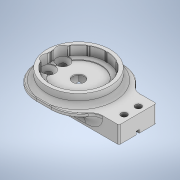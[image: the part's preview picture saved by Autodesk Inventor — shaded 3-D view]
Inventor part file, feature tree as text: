
AUTODESK INVENTOR PART (.ipt)
format: ipt  version: 2022 (Build 260153000, 153)  size: 1,263,104 bytes
history: native  units: mm
features: projected_geometry x17, extrude x13, sketch x12, fillet x8, other x6, pattern_circular x2, chamfer x1, revolve x1, mirror x1
ambient origin geometry x8: Origin, YZ Plane, XZ Plane, XY Plane, X Axis, Y Axis, Z Axis, Center Point
bodies: Body1 (feature_tree)
feature tree (61):
  other  "Твердое тело1"
  extrude  "Выдавливание1"  Depth=21.5mm
  extrude  "Выдавливание2"  Depth=41.0mm
  extrude  "Выдавливание3"  Depth=59.0mm
  extrude  "Выдавливание4"  Depth=10.6mm TaperAngle=0.0deg
  extrude  "Выдавливание5"  Depth=2.0mm
  extrude  "Выдавливание6"  Depth=4.4mm
  fillet  "Сопряжение1"  Radius=10600.0mm
  fillet  "Сопряжение2"  Radius=14.3mm
  fillet  "Сопряжение3"  Radius=10.0mm
  fillet  "Сопряжение4"  Radius=0.9mm
  extrude  "Выдавливание8"  Depth=150.0mm TaperAngle=0.0deg
  fillet  "Сопряжение6"  Radius=37.3mm
  other  "РабОсь1"
  fillet  "Сопряжение8"  Radius=2.5mm
  pattern_circular  "Круговой массив1"  [2 undecoded]
  extrude  "Выдавливание9"  Depth=3.0mm
  extrude  "Выдавливание10"  Depth=2.5mm TaperAngle=0.0deg
  fillet  "Сопряжение9"  Radius=20.0mm
  extrude  "Выдавливание11"  Depth=3.0mm
  chamfer  "Фаска1"  Distance=0.5mm
  extrude  "Выдавливание12"  Depth=1.0mm
  other  "РабОсь2"
  other  "РабПлоскость1"
  sketch  "Эскиз14"
  fillet  "Сопряжение11"  Radius=25.0mm
  extrude  "Выдавливание15"  Depth=0.7mm
  pattern_circular  "Круговой массив3"  Count=12 Angle=360.0deg
  revolve  "Вращение2"
  other  "РабПлоскость2"
  mirror  "Зеркальное отражение1"
  extrude  "Выдавливание17"  Depth=5.0mm TaperAngle=0.0deg
  sketch  "Эскиз1"
  sketch  "Эскиз2"
  sketch  "Эскиз3"
  projected_geometry  "Спроецированная петля1"
  sketch  "Эскиз5"
  projected_geometry  "Спроецированная петля2"
  sketch  "Эскиз6"
  projected_geometry  "Спроецированная петля3"
  projected_geometry  "Спроецированная петля4"
  projected_geometry  "Спроецированная петля5"
  sketch  "Эскиз9"
  sketch  "Эскиз10"
  projected_geometry  "Спроецированная петля6"
  sketch  "Эскиз12"
  projected_geometry  "Спроецированная петля7"
  projected_geometry  "Спроецированная петля8"
  sketch  "Эскиз13"
  other  "РабОсь3"
  sketch  "Эскиз17"
  projected_geometry  "Спроецированная петля9"
  projected_geometry  "Спроецированная петля10"
  projected_geometry  "Спроецированная петля11"
  projected_geometry  "Спроецированная петля12"
  projected_geometry  "Спроецированная петля13"
  projected_geometry  "Спроецированная петля14"
  projected_geometry  "Спроецированная петля15"
  projected_geometry  "Спроецированная петля16"
  sketch  "Эскиз18"
  projected_geometry  "Спроецированная петля17"
note: 2 required parameter values undecoded (feature->parameter linkage not recoverable at this tier; creation-order binding heuristic only, values carry confidence <= 0.55)
